# Revit family: Spout_Hob_Abey_PocoP_Basin_Short_Facebased
name_source: partatom
category: Plumbing Fixtures
units: mm (PartAtom-declared; Revit-internal decimal feet)

## family parameters
Cut with Voids When Loaded = No
Host = Face
Maintain Annotation Orientation = No
OmniClass Number = 23.31.11.00
OmniClass Title = Faucets
Part Type = Normal
Room Calculation Point = No
Round Connector Dimension = Use Diameter
Shared = No

## types (2) — shared parameters
Assembly Code = C1030210
CW Connection = Yes
Default Elevation = 0 mm
Description = Poco P Basin/Bath Hob 265mm Spout
HW Connection = Yes
IfcExportAs = IfcValve
IfcExportType = FAUCET
Manufacturer = Abey
ManufacturerOverallDepth = 183 mm
ManufacturerOverallHeight = 265 mm
ManufacturerOverallWidth = 54 mm
ManufacturerURLProductSpecific = https://www.abeyspecifier.com.au
ModifiedIssue = 20251103 $
URL = https://www.abey.com.au
Uniclass2015Code = Pr_40_20_87_55
Uniclass2015Title = Mixer taps
Uniclass2015Version = Products v1.38
Vent Connection = No
Waste Connection = No
zero-valued in all types: Cost

## per-type parameters (varying)
| type | ManufacturerSpecCode | Material | Model | Type Comments |
| Brushed Nickel Finish - (8HS145-BN-LF) | 8HS145-BN-LF | Metal_Abey_BrushedNickel | 8HS145-BN-LF | Spout - Hob - Brushed Nickel |
| Gun Metal Finish - (8HS145-GM-LF) | 8HS145-GM-LF | Metal_Abey_GunMetal | 8HS145-GM-LF | Spout - Hob - Gun Metal |

## geometry (parser evidence)
native form markers: Sweep x6
no freeform markers — native parametric forms only
